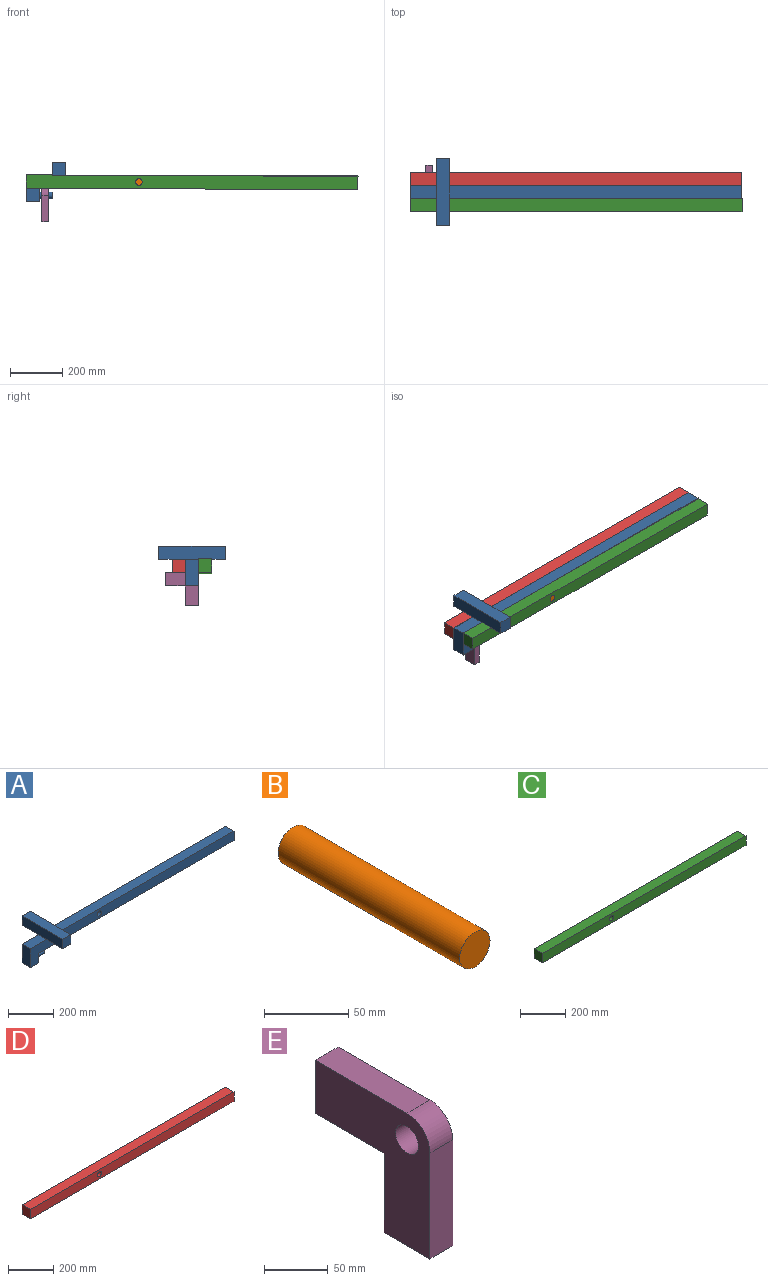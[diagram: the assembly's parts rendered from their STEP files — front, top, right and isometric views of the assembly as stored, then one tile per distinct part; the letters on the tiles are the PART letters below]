
ASSEMBLY  parts=5 mates=4
PART A: 19 faces, bbox 1270x254x152.4 mm
  f0: plane 1117.6x50.8mm, normal (0,0,1), area 56774.1mm2, adj f1,f2,f3,f11
  f1: plane 1270x101.6mm, normal (0,-1,0), area 66589.9mm2, adj f0,f2,f4,f5,f6,f13,f14,f15
  f2: plane 50.8x50.8mm, normal (1,0,0), area 2580.6mm2, adj f0,f1,f3,f6
  f3: plane 1270x101.6mm, normal (0,1,0), area 66589.9mm2, adj f0,f2,f4,f5,f6,f7,f14,f15
  f4: plane 101.6x50.8mm, normal (-1,0,0), area 5161.3mm2, adj f1,f3,f5,f16
  f5: plane 101.6x50.8mm, normal (0,0,1), area 5161.3mm2, adj f1,f3,f4,f9
  f6: plane 1219.2x50.8mm, normal (0,0,-1), area 61935.4mm2, adj f1,f2,f3,f15
  f7: plane 101.6x50.8mm, normal (0,0,-1), area 5161.3mm2, adj f3,f8,f9,f11
  f8: plane 50.8x50.8mm, normal (0,1,0), area 2580.6mm2, adj f7,f9,f11,f12
  f9: plane 254x50.8mm, normal (-1,0,0), area 12903.2mm2, adj f5,f7,f8,f10,f12,f13
  f10: plane 50.8x50.8mm, normal (0,-1,0), area 2580.6mm2, adj f9,f11,f12,f13
  f11: plane 254x50.8mm, normal (1,0,0), area 12903.2mm2, adj f0,f7,f8,f10,f12,f13
  f12: plane 254x50.8mm, normal (0,0,1), area 12903.2mm2, adj f8,f9,f10,f11
  f13: plane 101.6x50.8mm, normal (0,0,-1), area 5161.3mm2, adj f1,f9,f10,f11
  f14: cylinder r=12.7mm len=50.8mm, axis (0,-1,0), area 4053.7mm2, adj f1,f3
  f15: plane 50.8x50.8mm, normal (1,0,0), area 2073.9mm2, adj f1,f3,f6,f16,f17
  f16: plane 50.8x50.8mm, normal (0,0,-1), area 2580.6mm2, adj f1,f3,f4,f15
  f17: cylinder r=12.7mm len=50.8mm, axis (-1,0,0), area 4053.7mm2, adj f15,f18
  f18: plane 25.4x25.4mm, normal (1,0,0), area 506.7mm2, adj f17
PART B: 3 faces, bbox 25.4x152.4x25.4 mm
  f0: cylinder r=12.7mm len=152.4mm, axis (0,-1,0), area 12161mm2, adj f1,f2
  f1: plane 25.4x25.4mm, normal (0,1,0), area 506.7mm2, adj f0
  f2: plane 25.4x25.4mm, normal (0,-1,0), area 506.7mm2, adj f0
PART C: 7 faces, bbox 1270x50.8x50.8 mm
  f0: plane 1270x50.8mm, normal (0,-1,0), area 64009.3mm2, adj f1,f3,f4,f5,f6
  f1: plane 50.8x50.8mm, normal (1,0,0), area 2580.6mm2, adj f0,f2,f4,f5
  f2: plane 1270x50.8mm, normal (0,1,0), area 64009.3mm2, adj f1,f3,f4,f5,f6
  f3: plane 50.8x50.8mm, normal (-1,0,0), area 2580.6mm2, adj f0,f2,f4,f5
  f4: plane 1270x50.8mm, normal (0,0,1), area 64516mm2, adj f0,f1,f2,f3
  f5: plane 1270x50.8mm, normal (0,0,-1), area 64516mm2, adj f0,f1,f2,f3
  f6: cylinder r=12.7mm len=50.8mm, axis (0,-1,0), area 4053.7mm2, adj f0,f2
PART D: 7 faces, bbox 1270x50.8x50.8 mm
  f0: plane 50.8x50.8mm, normal (1,0,0), area 2580.6mm2, adj f1,f3,f4,f5
  f1: plane 1270x50.8mm, normal (0,1,0), area 64009.3mm2, adj f0,f2,f4,f5,f6
  f2: plane 50.8x50.8mm, normal (-1,0,0), area 2580.6mm2, adj f1,f3,f4,f5
  f3: plane 1270x50.8mm, normal (0,-1,0), area 64009.3mm2, adj f0,f2,f4,f5,f6
  f4: plane 1270x50.8mm, normal (0,0,1), area 64516mm2, adj f0,f1,f2,f3
  f5: plane 1270x50.8mm, normal (0,0,-1), area 64516mm2, adj f0,f1,f2,f3
  f6: cylinder r=12.7mm len=50.8mm, axis (0,-1,0), area 4053.7mm2, adj f1,f3
PART E: 10 faces, bbox 25.4x127x127 mm
  f0: plane 76.2x25.4mm, normal (0,1,0), area 1935.5mm2, adj f1,f5,f6,f7
  f1: plane 76.2x25.4mm, normal (0,0,-1), area 1935.5mm2, adj f0,f2,f6,f7
  f2: plane 50.8x25.4mm, normal (0,1,0), area 1290.3mm2, adj f1,f3,f6,f7
  f3: plane 101.6x25.4mm, normal (0,0,1), area 2580.6mm2, adj f2,f6,f7,f9
  f4: plane 101.6x25.4mm, normal (0,-1,0), area 2580.6mm2, adj f5,f6,f7,f9
  f5: plane 50.8x25.4mm, normal (0,0,-1), area 1290.3mm2, adj f0,f4,f6,f7
  f6: plane 127x127mm, normal (1,0,0), area 9677.4mm2, adj f0,f1,f2,f3,f4,f5,f8,f9
  f7: plane 127x127mm, normal (-1,0,0), area 9677.4mm2, adj f0,f1,f2,f3,f4,f5,f8,f9
  f8: cylinder r=12.7mm len=25.4mm, axis (1,0,0), area 2026.8mm2, adj f6,f7
  f9: cylinder r=25.4mm len=25.4mm, axis (1,0,0), area 1013.4mm2, adj f3,f4,f6,f7
PLACE A t=(0,-25.4,0)mm
PLACE B at identity fixed
PLACE C rot(axis=(0,1,0),0.3deg) t=(-0.12,0,-0.98)mm
PLACE D t=(0,-50.8,0)mm
PLACE E t=(-2.85,-25.4,0)mm
MATE cylindrical A.f14 <-> B.f0  axis (0,-1,0) through (-203.2,-25.4,25.4)mm
MATE cylindrical A.f17 <-> E.f8  axis (-1,0,0) through (-558.8,-25.4,-25.4)mm
MATE cylindrical D.f6 <-> B.f0  axis (0,-1,0) through (-203.2,50.8,25.4)mm
MATE cylindrical C.f6 <-> B.f0  axis (0,-1,0) through (-203.2,-101.6,25.4)mm
